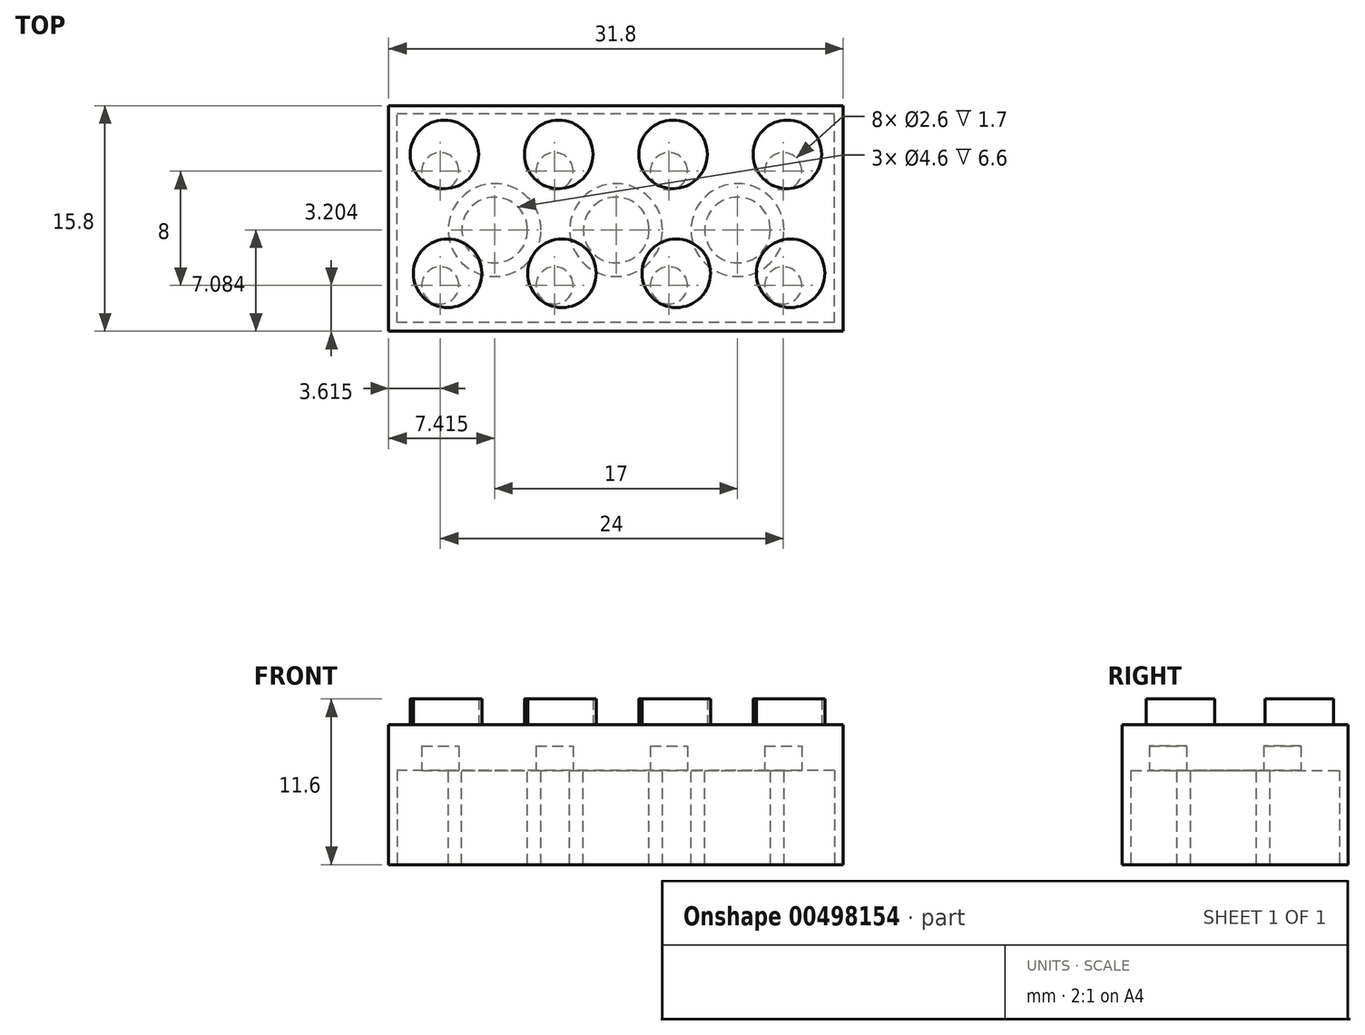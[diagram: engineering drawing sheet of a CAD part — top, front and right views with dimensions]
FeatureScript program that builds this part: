
annotation { "Feature Type Name" : "Feature", "Feature Type Description" : "" }
export const myFeature = defineFeature(function(context is Context, id is Id, definition is map)
    precondition{}
    {
        {
            var Q0;
            Q0=qCreatedBy(makeId("Top.planeOp"),FACE);
            var sketch = newSketch(context, id + "F0", { "sketchPlane" : qUnion([Q0])});
            skLineSegment(sketch, "E0.bottom", {"start": v(0, 15.8) * mm, "end": v(31.8, 15.8) * mm});
            skLineSegment(sketch, "E0.top", {"start": v(0, 0) * mm, "end": v(31.8, 0) * mm});
            skLineSegment(sketch, "E0.left", {"start": v(0, 15.8) * mm, "end": v(0, 0) * mm});
            skLineSegment(sketch, "E0.right", {"start": v(31.8, 15.8) * mm, "end": v(31.8, 0) * mm});
            skSolve(sketch);
        }
        {
            var Q0;
            Q0=makeQuery(id+"F0.imprint","IMPRINT",FACE,{"disambiguationData":[TD([[makeQuery(id+"F0.imprint","IMPRINT",EDGE,{"derivedFrom":sQuery(id+"F0.wireOp",EDGE,"E0.bottom")}),-1.0]])]});
            extrude(context, id + "F1", {"entities" : qUnion([Q0]), "depth" : 9.8 * mm});
        }
        {
            var Q0;
            Q0=makeQuery(id+"F1.opExtrude","CAP_FACE",FACE,{"disambiguationData":[OSD([sQuery(id+"F0.wireOp",EDGE,"E0.bottom"),sQuery(id+"F0.wireOp",EDGE,"E0.top"),sQuery(id+"F0.wireOp",EDGE,"E0.left"),sQuery(id+"F0.wireOp",EDGE,"E0.right")])],"isStart":false});
            var sketch = newSketch(context, id + "F2", { "sketchPlane" : qUnion([Q0])});
            skCircle(sketch, "E1", {"center": v(3.9, 12.38) * mm, "radius": 2.4 * mm});
            skCircle(sketch, "E2.1.0.0", {"center": v(11.9, 12.38) * mm, "radius": 2.4 * mm});
            skCircle(sketch, "E2.2.0.0", {"center": v(19.9, 12.38) * mm, "radius": 2.4 * mm});
            skCircle(sketch, "E2.3.0.0", {"center": v(27.9, 12.38) * mm, "radius": 2.4 * mm});
            skLineSegment(sketch, "E2.direction1", {"start": v(3.9, 12.38) * mm, "end": v(11.9, 12.38) * mm, "construction": true});
            skCircle(sketch, "E3", {"center": v(4.12, 4.06) * mm, "radius": 2.4 * mm});
            skCircle(sketch, "E4.1.0.0", {"center": v(12.12, 4.06) * mm, "radius": 2.4 * mm});
            skCircle(sketch, "E4.2.0.0", {"center": v(20.12, 4.06) * mm, "radius": 2.4 * mm});
            skCircle(sketch, "E4.3.0.0", {"center": v(28.12, 4.06) * mm, "radius": 2.4 * mm});
            skLineSegment(sketch, "E4.direction1", {"start": v(4.12, 4.06) * mm, "end": v(12.12, 4.06) * mm, "construction": true});
            skSolve(sketch);
        }
        {
            var Q0;
            Q0=makeQuery(id+"F2.imprint","IMPRINT",FACE,{"disambiguationData":[TD([[makeQuery(id+"F2.imprint","IMPRINT",EDGE,{"derivedFrom":sQuery(id+"F2.wireOp",EDGE,"E1")}),1.0]])]});
            var Q1;
            Q1=makeQuery(id+"F2.imprint","IMPRINT",FACE,{"disambiguationData":[TD([[makeQuery(id+"F2.imprint","IMPRINT",EDGE,{"derivedFrom":sQuery(id+"F2.wireOp",EDGE,"E4.3.0.0")}),1.0]])]});
            var Q2;
            Q2=makeQuery(id+"F2.imprint","IMPRINT",FACE,{"disambiguationData":[TD([[makeQuery(id+"F2.imprint","IMPRINT",EDGE,{"derivedFrom":sQuery(id+"F2.wireOp",EDGE,"E2.3.0.0")}),1.0]])]});
            var Q3;
            Q3=makeQuery(id+"F2.imprint","IMPRINT",FACE,{"disambiguationData":[TD([[makeQuery(id+"F2.imprint","IMPRINT",EDGE,{"derivedFrom":sQuery(id+"F2.wireOp",EDGE,"E2.2.0.0")}),1.0]])]});
            var Q4;
            Q4=makeQuery(id+"F2.imprint","IMPRINT",FACE,{"disambiguationData":[TD([[makeQuery(id+"F2.imprint","IMPRINT",EDGE,{"derivedFrom":sQuery(id+"F2.wireOp",EDGE,"E4.2.0.0")}),1.0]])]});
            var Q5;
            Q5=makeQuery(id+"F2.imprint","IMPRINT",FACE,{"disambiguationData":[TD([[makeQuery(id+"F2.imprint","IMPRINT",EDGE,{"derivedFrom":sQuery(id+"F2.wireOp",EDGE,"E2.1.0.0")}),1.0]])]});
            var Q6;
            Q6=makeQuery(id+"F2.imprint","IMPRINT",FACE,{"disambiguationData":[TD([[makeQuery(id+"F2.imprint","IMPRINT",EDGE,{"derivedFrom":sQuery(id+"F2.wireOp",EDGE,"E4.1.0.0")}),1.0]])]});
            var Q7;
            Q7=makeQuery(id+"F2.imprint","IMPRINT",FACE,{"disambiguationData":[TD([[makeQuery(id+"F2.imprint","IMPRINT",EDGE,{"derivedFrom":sQuery(id+"F2.wireOp",EDGE,"E3")}),1.0]])]});
            extrude(context, id + "F3", {"entities" : qUnion([Q0, Q1, Q2, Q3, Q4, Q5, Q6, Q7]), "operationType" : NewBodyOperationType.ADD, "depth" : 1.8 * mm});
        }
        {
            var Q0;
            Q0=makeQuery(id+"F1.opExtrude","CAP_FACE",FACE,{"disambiguationData":[OSD([sQuery(id+"F0.wireOp",EDGE,"E0.bottom"),sQuery(id+"F0.wireOp",EDGE,"E0.top"),sQuery(id+"F0.wireOp",EDGE,"E0.left"),sQuery(id+"F0.wireOp",EDGE,"E0.right")])],"isStart":true});
            var sketch = newSketch(context, id + "F4", { "sketchPlane" : qUnion([Q0])});
            skLineSegment(sketch, "E5.bottom", {"start": v(31.2, -0.6) * mm, "end": v(0.6, -0.6) * mm});
            skLineSegment(sketch, "E5.top", {"start": v(31.2, -15.2) * mm, "end": v(0.6, -15.2) * mm});
            skLineSegment(sketch, "E5.left", {"start": v(31.2, -0.6) * mm, "end": v(31.2, -15.2) * mm});
            skLineSegment(sketch, "E5.right", {"start": v(0.6, -0.6) * mm, "end": v(0.6, -15.2) * mm});
            skPoint(sketch, "E5.middle", {"position": v(15.9, -7.9) * mm});
            skPoint(sketch, "E5.middle.positionSnap0", {"position": v(15.9, 0) * mm});
            skPoint(sketch, "E5.middle.positionSnap1", {"position": v(31.8, -7.9) * mm});
            skPoint(sketch, "E5.centerSnap0", {"position": v(15.9, 0) * mm});
            skPoint(sketch, "E5.centerSnap1", {"position": v(31.8, -7.9) * mm});
            skSolve(sketch);
        }
        {
            var Q0;
            Q0=makeQuery(id+"F4.imprint","IMPRINT",FACE,{"disambiguationData":[TD([[makeQuery(id+"F4.imprint","IMPRINT",EDGE,{"derivedFrom":sQuery(id+"F4.wireOp",EDGE,"E5.bottom")}),1.0]])]});
            extrude(context, id + "F5", {"entities" : qUnion([Q0]), "operationType" : NewBodyOperationType.REMOVE, "oppositeDirection" : true, "depth" : 6.6 * mm});
        }
        {
            var Q0;
            Q0=makeQuery(id+"F5.boolean.opBoolean","COPY",FACE,{"derivedFrom":makeQuery(id+"F5.opExtrude","CAP_FACE",FACE,{"disambiguationData":[OSD([sQuery(id+"F4.wireOp",EDGE,"E5.bottom"),sQuery(id+"F4.wireOp",EDGE,"E5.top"),sQuery(id+"F4.wireOp",EDGE,"E5.left"),sQuery(id+"F4.wireOp",EDGE,"E5.right")])],"isStart":false})});
            var sketch = newSketch(context, id + "F6", { "sketchPlane" : qUnion([Q0])});
            skCircle(sketch, "E6", {"center": v(3.61, -3.2) * mm, "radius": 1.3 * mm});
            skCircle(sketch, "E7.0.1.0", {"center": v(3.61, -11.2) * mm, "radius": 1.3 * mm});
            skCircle(sketch, "E7.1.0.0", {"center": v(11.61, -3.2) * mm, "radius": 1.3 * mm});
            skCircle(sketch, "E7.1.1.0", {"center": v(11.61, -11.2) * mm, "radius": 1.3 * mm});
            skCircle(sketch, "E7.2.0.0", {"center": v(19.61, -3.2) * mm, "radius": 1.3 * mm});
            skCircle(sketch, "E7.2.1.0", {"center": v(19.61, -11.2) * mm, "radius": 1.3 * mm});
            skCircle(sketch, "E7.3.0.0", {"center": v(27.61, -3.2) * mm, "radius": 1.3 * mm});
            skCircle(sketch, "E7.3.1.0", {"center": v(27.61, -11.2) * mm, "radius": 1.3 * mm});
            skLineSegment(sketch, "E7.direction1", {"start": v(3.61, -3.2) * mm, "end": v(11.61, -3.2) * mm, "construction": true});
            skLineSegment(sketch, "E7.direction2", {"start": v(3.61, -3.2) * mm, "end": v(3.61, -11.2) * mm, "construction": true});
            skSolve(sketch);
        }
        {
            var Q0;
            Q0=makeQuery(id+"F6.imprint","IMPRINT",FACE,{"disambiguationData":[TD([[makeQuery(id+"F6.imprint","IMPRINT",EDGE,{"derivedFrom":sQuery(id+"F6.wireOp",EDGE,"E6")}),1.0]])]});
            var Q1;
            Q1=makeQuery(id+"F6.imprint","IMPRINT",FACE,{"disambiguationData":[TD([[makeQuery(id+"F6.imprint","IMPRINT",EDGE,{"derivedFrom":sQuery(id+"F6.wireOp",EDGE,"E7.1.0.0")}),1.0]])]});
            var Q2;
            Q2=makeQuery(id+"F6.imprint","IMPRINT",FACE,{"disambiguationData":[TD([[makeQuery(id+"F6.imprint","IMPRINT",EDGE,{"derivedFrom":sQuery(id+"F6.wireOp",EDGE,"E7.2.0.0")}),1.0]])]});
            var Q3;
            Q3=makeQuery(id+"F6.imprint","IMPRINT",FACE,{"disambiguationData":[TD([[makeQuery(id+"F6.imprint","IMPRINT",EDGE,{"derivedFrom":sQuery(id+"F6.wireOp",EDGE,"E7.3.0.0")}),1.0]])]});
            var Q4;
            Q4=makeQuery(id+"F6.imprint","IMPRINT",FACE,{"disambiguationData":[TD([[makeQuery(id+"F6.imprint","IMPRINT",EDGE,{"derivedFrom":sQuery(id+"F6.wireOp",EDGE,"E7.3.1.0")}),1.0]])]});
            var Q5;
            Q5=makeQuery(id+"F6.imprint","IMPRINT",FACE,{"disambiguationData":[TD([[makeQuery(id+"F6.imprint","IMPRINT",EDGE,{"derivedFrom":sQuery(id+"F6.wireOp",EDGE,"E7.2.1.0")}),1.0]])]});
            var Q6;
            Q6=makeQuery(id+"F6.imprint","IMPRINT",FACE,{"disambiguationData":[TD([[makeQuery(id+"F6.imprint","IMPRINT",EDGE,{"derivedFrom":sQuery(id+"F6.wireOp",EDGE,"E7.1.1.0")}),1.0]])]});
            var Q7;
            Q7=makeQuery(id+"F6.imprint","IMPRINT",FACE,{"disambiguationData":[TD([[makeQuery(id+"F6.imprint","IMPRINT",EDGE,{"derivedFrom":sQuery(id+"F6.wireOp",EDGE,"E7.0.1.0")}),1.0]])]});
            extrude(context, id + "F7", {"entities" : qUnion([Q0, Q1, Q2, Q3, Q4, Q5, Q6, Q7]), "operationType" : NewBodyOperationType.REMOVE, "oppositeDirection" : true, "depth" : 1.7 * mm});
        }
        {
            var Q0;
            Q0=makeQuery(id+"F5.boolean.opBoolean","COPY",FACE,{"derivedFrom":makeQuery(id+"F5.opExtrude","CAP_FACE",FACE,{"disambiguationData":[OSD([sQuery(id+"F4.wireOp",EDGE,"E5.bottom"),sQuery(id+"F4.wireOp",EDGE,"E5.top"),sQuery(id+"F4.wireOp",EDGE,"E5.left"),sQuery(id+"F4.wireOp",EDGE,"E5.right")])],"isStart":false})});
            var sketch = newSketch(context, id + "F8", { "sketchPlane" : qUnion([Q0])});
            skCircle(sketch, "E8", {"center": v(7.41, -7.08) * mm, "radius": 3.25 * mm});
            skCircle(sketch, "E9.1.0.0", {"center": v(15.91, -7.08) * mm, "radius": 3.25 * mm});
            skCircle(sketch, "E9.2.0.0", {"center": v(24.41, -7.08) * mm, "radius": 3.25 * mm});
            skLineSegment(sketch, "E9.direction1", {"start": v(7.41, -7.08) * mm, "end": v(15.91, -7.08) * mm, "construction": true});
            skCircle(sketch, "E10", {"center": v(7.41, -7.08) * mm, "radius": 2.3 * mm});
            skCircle(sketch, "E11.1.0.0", {"center": v(15.91, -7.08) * mm, "radius": 2.3 * mm});
            skCircle(sketch, "E11.2.0.0", {"center": v(24.41, -7.08) * mm, "radius": 2.3 * mm});
            skSolve(sketch);
        }
        {
            var Q0;
            Q0=makeQuery(id+"F8.imprint","IMPRINT",FACE,{"disambiguationData":[TD([[makeQuery(id+"F8.imprint","IMPRINT",EDGE,{"derivedFrom":sQuery(id+"F8.wireOp",EDGE,"E8")}),1.0]])]});
            var Q1;
            Q1=makeQuery(id+"F8.imprint","IMPRINT",FACE,{"disambiguationData":[TD([[makeQuery(id+"F8.imprint","IMPRINT",EDGE,{"derivedFrom":sQuery(id+"F8.wireOp",EDGE,"E9.1.0.0")}),1.0]])]});
            var Q2;
            Q2=makeQuery(id+"F8.imprint","IMPRINT",FACE,{"disambiguationData":[TD([[makeQuery(id+"F8.imprint","IMPRINT",EDGE,{"derivedFrom":sQuery(id+"F8.wireOp",EDGE,"E9.2.0.0")}),1.0]])]});
            extrude(context, id + "F9", {"entities" : qUnion([Q0, Q1, Q2]), "operationType" : NewBodyOperationType.ADD, "depth" : 6.6 * mm});
        }
    });
